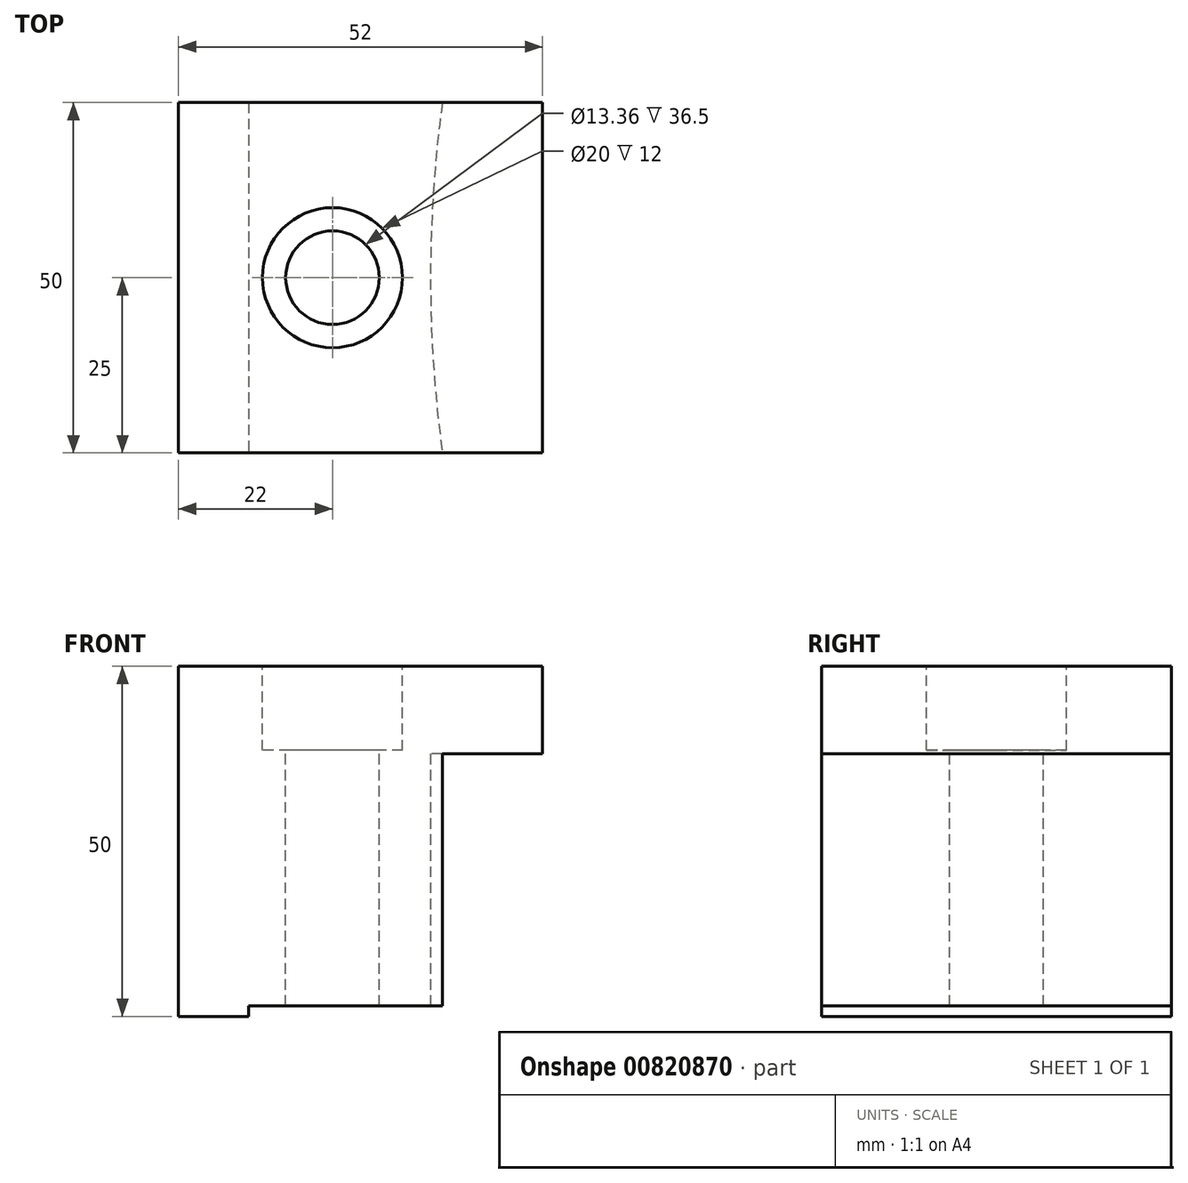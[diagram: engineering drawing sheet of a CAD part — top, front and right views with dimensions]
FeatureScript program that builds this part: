
annotation { "Feature Type Name" : "Feature", "Feature Type Description" : "" }
export const myFeature = defineFeature(function(context is Context, id is Id, definition is map)
    precondition{}
    {
        {
            var Q0;
            Q0=qCreatedBy(makeId("Right.planeOp"),FACE);
            var sketch = newSketch(context, id + "F0", { "sketchPlane" : qUnion([Q0])});
            skLineSegment(sketch, "E0.bottom", {"start": v(0, 0) * mm, "end": v(-50, 0) * mm});
            skLineSegment(sketch, "E0.top", {"start": v(0, 50) * mm, "end": v(-50, 50) * mm});
            skLineSegment(sketch, "E0.left", {"start": v(0, 0) * mm, "end": v(0, 50) * mm});
            skLineSegment(sketch, "E0.right", {"start": v(-50, 0) * mm, "end": v(-50, 50) * mm});
            skSolve(sketch);
        }
        {
            var Q0;
            Q0 = qSketchRegion(id + "F0", true);
            extrude(context, id + "F1", {"entities" : qUnion([Q0]), "depth" : 52 * mm, "offsetDistance" : 25 * mm});
        }
        {
            var Q0;
            Q0=makeQuery(id+"F1.opExtrude","CAP_FACE",FACE,{"disambiguationData":[OSD([sQuery(id+"F0.wireOp",EDGE,"E0.bottom"),sQuery(id+"F0.wireOp",EDGE,"E0.top"),sQuery(id+"F0.wireOp",EDGE,"E0.left"),sQuery(id+"F0.wireOp",EDGE,"E0.right")])],"isStart":false});
            var sketch = newSketch(context, id + "F2", { "sketchPlane" : qUnion([Q0])});
            skLineSegment(sketch, "E1.bottom", {"start": v(-50, 0) * mm, "end": v(0, 0) * mm});
            skLineSegment(sketch, "E1.top", {"start": v(-50, 1.5) * mm, "end": v(0, 1.5) * mm});
            skLineSegment(sketch, "E1.left", {"start": v(-50, 0) * mm, "end": v(-50, 1.5) * mm});
            skLineSegment(sketch, "E1.right", {"start": v(0, 0) * mm, "end": v(0, 1.5) * mm});
            skSolve(sketch);
        }
        {
            var Q0;
            Q0 = qSketchRegion(id + "F2", true);
            extrude(context, id + "F3", {"entities" : qUnion([Q0]), "operationType" : NewBodyOperationType.REMOVE, "oppositeDirection" : true, "depth" : 42 * mm, "offsetDistance" : 25 * mm});
        }
        {
            var Q0;
            Q0=makeQuery(id+"F3.boolean.opBoolean","COPY",FACE,{"derivedFrom":makeQuery(id+"F3.opExtrude","SWEPT_FACE",FACE,{"disambiguationData":[OSD([sQuery(id+"F2.wireOp",EDGE,"E1.top")])]})});
            var sketch = newSketch(context, id + "F4", { "sketchPlane" : qUnion([Q0])});
            skArc(sketch, "E2", {"start": v(77.26, 141.64) * mm, "mid": v(36.13, 31.92) * mm, "end": v(68.97, -80.57) * mm});
            skLineSegment(sketch, "E3", {"start": v(68.97, -80.57) * mm, "end": v(77.26, 141.64) * mm});
            skSolve(sketch);
        }
        {
            var Q0;
            Q0 = qSketchRegion(id + "F4", true);
            extrude(context, id + "F5", {"entities" : qUnion([Q0]), "operationType" : NewBodyOperationType.REMOVE, "oppositeDirection" : true, "depth" : 36 * mm, "offsetDistance" : 25 * mm});
        }
        {
            var Q0;
            Q0=makeQuery(id+"F1.opExtrude","SWEPT_FACE",FACE,{"disambiguationData":[OSD([sQuery(id+"F0.wireOp",EDGE,"E0.top")])]});
            var sketch = newSketch(context, id + "F6", { "sketchPlane" : qUnion([Q0])});
            skCircle(sketch, "E4", {"center": v(22, -25) * mm, "radius": 6.68 * mm});
            skSolve(sketch);
        }
        {
            var Q0;
            Q0 = qSketchRegion(id + "F6", true);
            extrude(context, id + "F7", {"entities" : qUnion([Q0]), "operationType" : NewBodyOperationType.REMOVE, "oppositeDirection" : true, "depth" : 65.6 * mm, "offsetDistance" : 25 * mm});
        }
        {
            var Q0;
            Q0=makeQuery(id+"F1.opExtrude","SWEPT_FACE",FACE,{"disambiguationData":[OSD([sQuery(id+"F0.wireOp",EDGE,"E0.top")])]});
            var sketch = newSketch(context, id + "F8", { "sketchPlane" : qUnion([Q0])});
            skCircle(sketch, "E5", {"center": v(22, -25) * mm, "radius": 10 * mm});
            skSolve(sketch);
        }
        {
            var Q0;
            Q0 = qSketchRegion(id + "F8", true);
            extrude(context, id + "F9", {"entities" : qUnion([Q0]), "operationType" : NewBodyOperationType.REMOVE, "oppositeDirection" : true, "depth" : 12 * mm, "offsetDistance" : 25 * mm});
        }
    });
